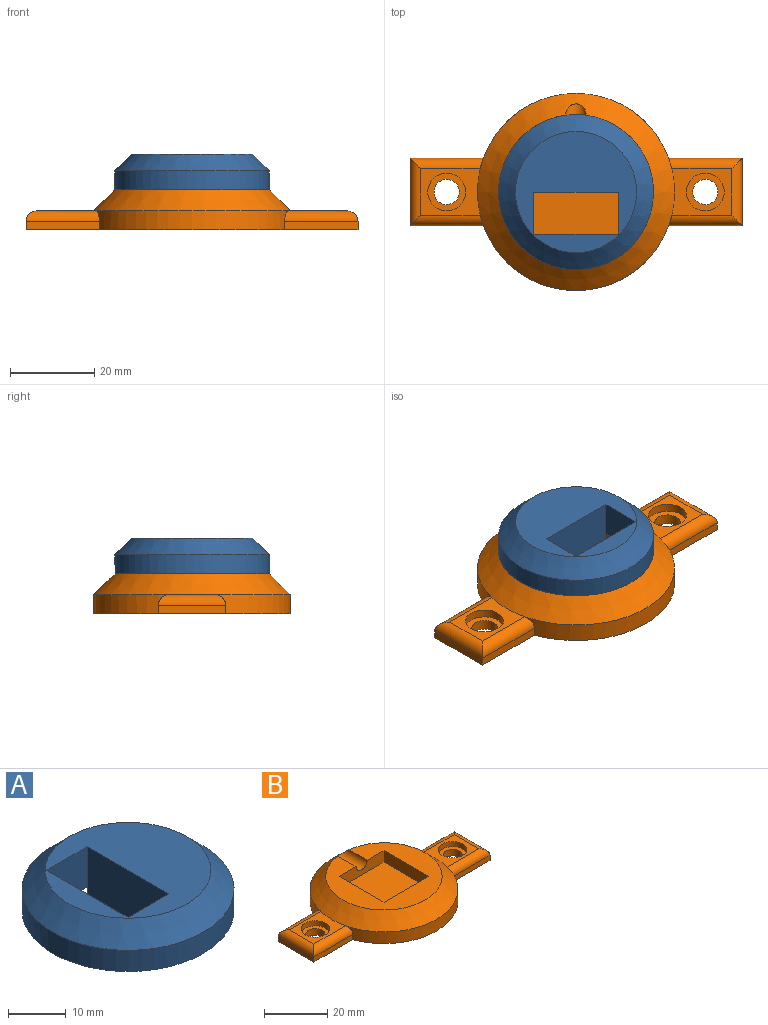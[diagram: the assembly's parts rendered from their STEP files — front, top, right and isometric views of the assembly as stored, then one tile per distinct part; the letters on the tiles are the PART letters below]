
ASSEMBLY  parts=2 mates=1
PART A: 17 faces, bbox 36.8x36.8x10 mm
  f0: plane 10x8.5mm, normal (0,1,0), area 85mm2, adj f4,f5,f9,f11
  f1: plane 10x8.5mm, normal (0,-1,0), area 85mm2, adj f4,f5,f9,f11
  f2: plane 20x6.85mm, normal (0,0,-1), area 136.9mm2, adj f3,f8,f10,f13
  f3: plane 6.85x4.5mm, normal (0,1,0), area 30.8mm2, adj f2,f5,f8,f13
  f4: plane 28.76x28.76mm, normal (0,0,1), area 449.6mm2, adj f0,f1,f7,f9,f11
  f5: plane 36.76x36.59mm, normal (0,0,-1), area 619.7mm2, adj f0,f1,f3,f6,f8,f9,f10,f12
  f6: cylinder r=18.38mm len=36.76mm, axis (0,0,-1), area 509.8mm2, adj f5,f7,f12
  f7: cone r=14.38mm half-angle=45deg, axis (0,0,-1), area 582.2mm2, adj f4,f6
  f8: plane 20x4.5mm, normal (-1,0,0), area 80.2mm2, adj f2,f3,f5,f10,f12
  f9: plane 20x8.5mm, normal (1,0,0), area 170mm2, adj f0,f1,f4,f5
  f10: plane 6.85x4.5mm, normal (0,-1,0), area 30.8mm2, adj f2,f5,f8,f13
  f11: plane 20x10mm, normal (-1,0,0), area 200mm2, adj f0,f1,f4,f14,f15,f16
  f12: cylinder r=2.5mm len=8.38mm, axis (-1,0,0), area 65.1mm2, adj f5,f6,f8
  f13: plane 20x6mm, normal (1,0,0), area 120mm2, adj f2,f3,f10,f14,f15,f16
  f14: plane 3.16x1.5mm, normal (0,-1,0), area 4.7mm2, adj f5,f11,f13,f16
  f15: plane 3.16x1.5mm, normal (0,1,0), area 4.7mm2, adj f5,f11,f13,f16
  f16: plane 20x3.16mm, normal (0,0,-1), area 63.1mm2, adj f11,f13,f14,f15
PART B: 31 faces, bbox 78.8x46.8x9.5 mm
  f0: cylinder r=3mm len=6mm, axis (0,0,1), area 47.1mm2, adj f4,f30
  f1: cylinder r=3mm len=6mm, axis (0,0,1), area 47.1mm2, adj f4,f28
  f2: cylinder r=23.38mm len=45.46mm, axis (0,0,-1), area 259.9mm2, adj f4,f12,f13,f17,f21,f24
  f3: cylinder r=23.38mm len=45.46mm, axis (0,0,-1), area 259.9mm2, adj f4,f12,f14,f18,f23,f26
  f4: plane 78.77x46.77mm, normal (0,0,-1), area 2188.3mm2, adj f0,f1,f2,f3,f13,f14,f15,f17
  f5: plane 20x4.5mm, normal (1,0,0), area 90mm2, adj f6,f8,f9,f10
  f6: plane 20x4.5mm, normal (0,-1,0), area 80.2mm2, adj f5,f7,f9,f10,f11
  f7: plane 20x4.5mm, normal (-1,0,0), area 90mm2, adj f6,f8,f9,f10
  f8: plane 20x4.5mm, normal (0,1,0), area 90mm2, adj f5,f7,f9,f10
  f9: plane 36.77x36.6mm, normal (0,0,1), area 620.2mm2, adj f5,f6,f7,f8,f11,f12
  f10: plane 20x20mm, normal (0,0,1), area 400mm2, adj f5,f6,f7,f8
  f11: cylinder r=2.5mm len=10.89mm, axis (0,-1,0), area 77.7mm2, adj f6,f9,f12
  f12: cone r=18.38mm half-angle=45deg, axis (0,0,-1), area 914mm2, adj f2,f3,f9,f11,f16,f20
  f13: plane 17.41x2mm, normal (0,-1,0), area 34.8mm2, adj f2,f4,f15,f24
  f14: plane 17.41x2mm, normal (0,1,0), area 34.8mm2, adj f3,f4,f15,f26
  f15: plane 16x2mm, normal (-1,0,0), area 32mm2, adj f4,f13,f14,f25
  f16: plane 14.16x11mm, normal (0,0,1), area 87.3mm2, adj f12,f24,f25,f26,f29
  f17: plane 17.41x2mm, normal (0,-1,0), area 34.8mm2, adj f2,f4,f19,f21
  f18: plane 17.41x2mm, normal (0,1,0), area 34.8mm2, adj f3,f4,f19,f23
  f19: plane 16x2mm, normal (1,0,0), area 32mm2, adj f4,f17,f18,f22
  f20: plane 14.16x11mm, normal (0,0,1), area 87.3mm2, adj f12,f21,f22,f23,f27
  f21: cylinder r=2.5mm len=17.41mm, axis (1,0,0), area 63.6mm2, adj f2,f17,f20,f22
  f22: cylinder r=2.5mm len=16mm, axis (0,1,0), area 55.7mm2, adj f19,f20,f21,f23
  f23: cylinder r=2.5mm len=17.41mm, axis (-1,0,0), area 63.6mm2, adj f3,f18,f20,f22
  f24: cylinder r=2.5mm len=17.41mm, axis (-1,0,0), area 63.6mm2, adj f2,f13,f16,f25
  f25: cylinder r=2.5mm len=16mm, axis (0,1,0), area 55.7mm2, adj f15,f16,f24,f26
  f26: cylinder r=2.5mm len=17.41mm, axis (1,0,0), area 63.6mm2, adj f3,f14,f16,f25
  f27: cylinder r=4.5mm len=9mm, axis (0,0,1), area 56.5mm2, adj f20,f28
  f28: plane 9x9mm, normal (0,0,1), area 35.3mm2, adj f1,f27
  f29: cylinder r=4.5mm len=9mm, axis (0,0,1), area 56.5mm2, adj f16,f30
  f30: plane 9x9mm, normal (0,0,1), area 35.3mm2, adj f0,f29
PLACE A rot(axis=(0,0,1),90deg) t=(0,-0.05,5.5)mm
PLACE B t=(0,0,-4)mm
MATE planar A.f5 <-> B.f9  axis (0,0,-1) through (10,-5.05,5.5)mm
